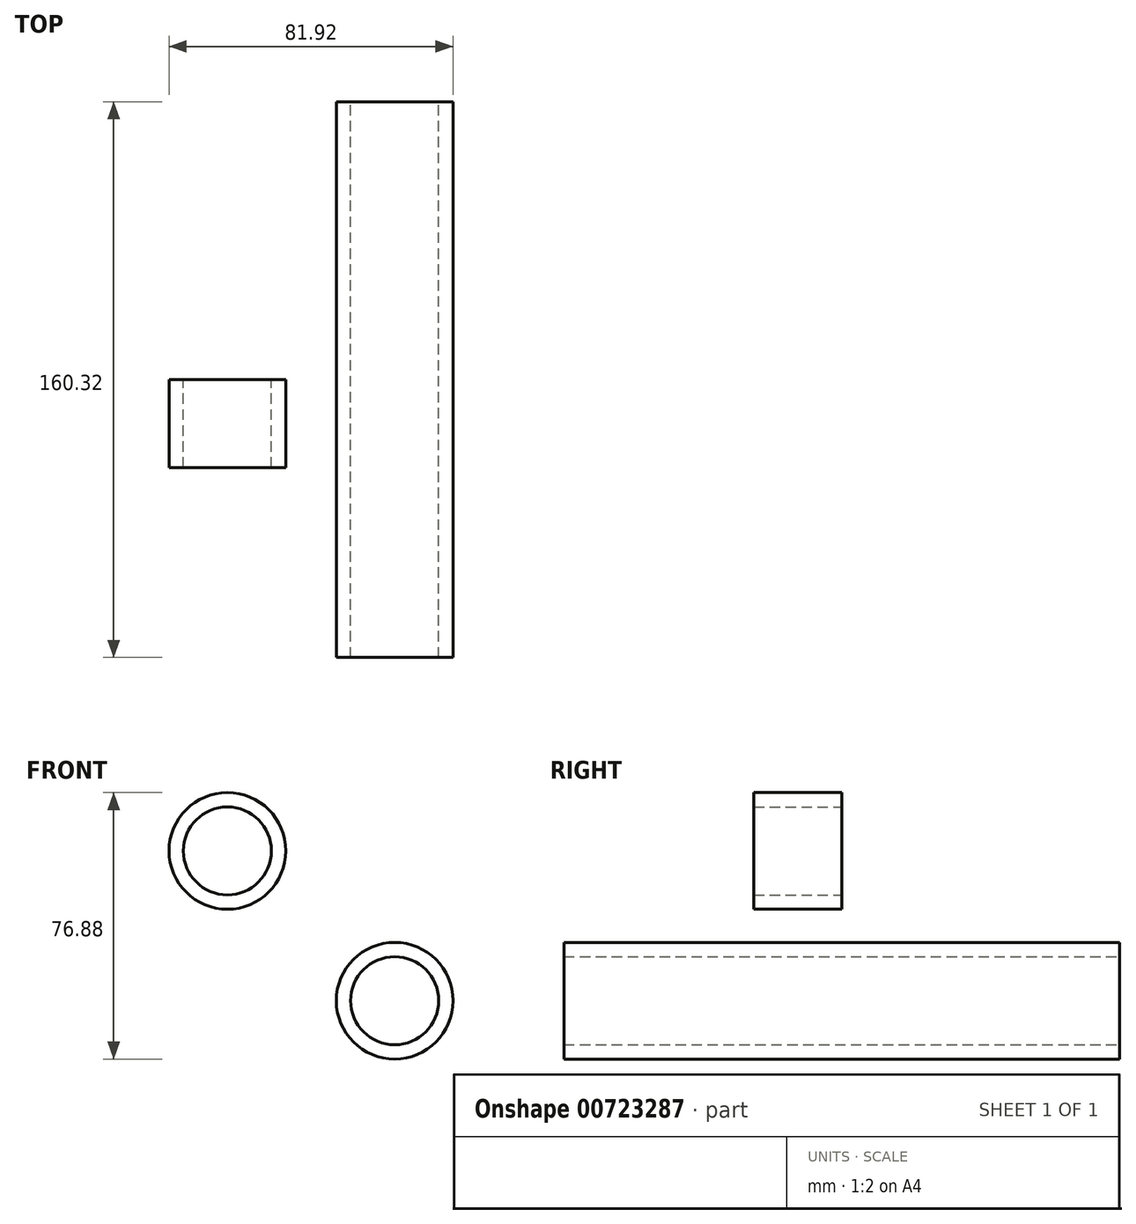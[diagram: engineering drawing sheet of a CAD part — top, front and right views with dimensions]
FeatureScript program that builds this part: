
annotation { "Feature Type Name" : "Feature", "Feature Type Description" : "" }
export const myFeature = defineFeature(function(context is Context, id is Id, definition is map)
    precondition{}
    {
        {
            var Q0;
            Q0=qCreatedBy(makeId("Front.planeOp"),FACE);
            var sketch = newSketch(context, id + "F0", { "sketchPlane" : qUnion([Q0])});
            skCircle(sketch, "E0", {"center": v(0, 0) * mm, "radius": 12.7 * mm});
            skCircle(sketch, "E1", {"center": v(0, 0) * mm, "radius": 16.83 * mm});
            skSolve(sketch);
        }
        {
            var Q0;
            Q0 = qSketchRegion(id + "F0", true);
            extrude(context, id + "F1", {"entities" : qUnion([Q0]), "endBound" : BoundingType.SYMMETRIC, "depth" : 160.32 * mm, "offsetDistance" : 25.4 * mm});
        }
        {
            var Q0;
            Q0=qCreatedBy(makeId("Front.planeOp"),FACE);
            var sketch = newSketch(context, id + "F2", { "sketchPlane" : qUnion([Q0])});
            skCircle(sketch, "E2", {"center": v(-48.26, 43.22) * mm, "radius": 12.7 * mm});
            skCircle(sketch, "E3", {"center": v(-48.26, 43.22) * mm, "radius": 16.83 * mm});
            skSolve(sketch);
        }
        {
            var Q0;
            Q0 = qSketchRegion(id + "F2", true);
            extrude(context, id + "F3", {"entities" : qUnion([Q0]), "depth" : 25.4 * mm, "offsetDistance" : 25.4 * mm});
        }
    });
